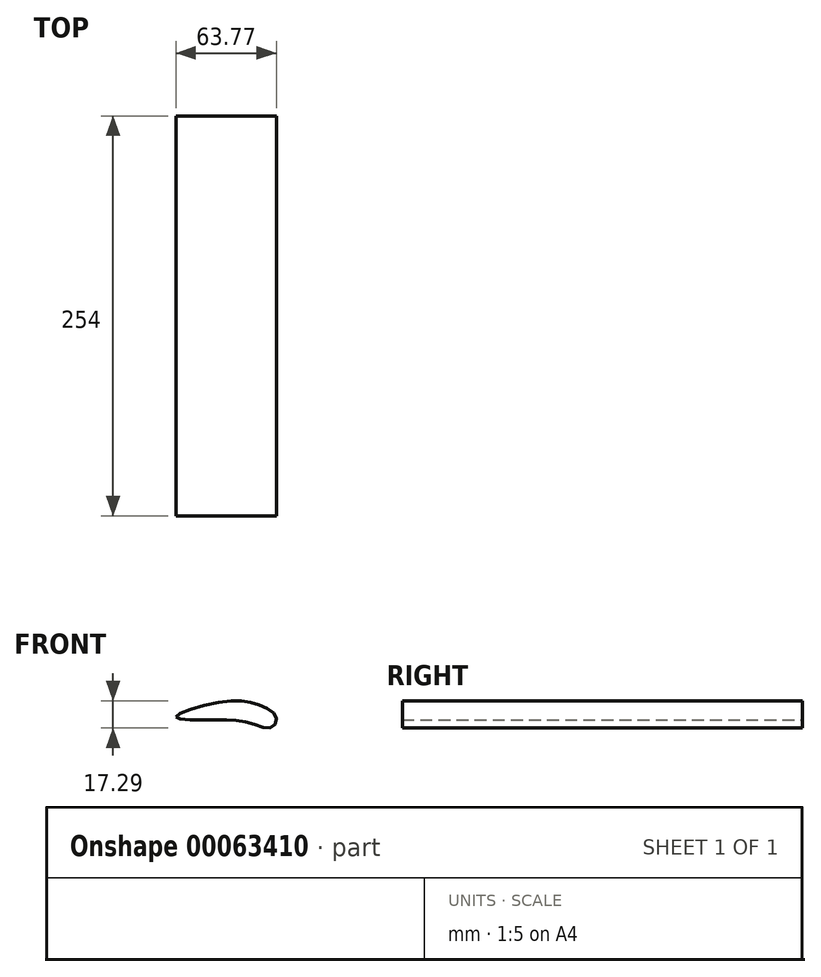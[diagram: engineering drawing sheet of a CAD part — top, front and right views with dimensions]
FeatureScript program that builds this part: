
annotation { "Feature Type Name" : "Feature", "Feature Type Description" : "" }
export const myFeature = defineFeature(function(context is Context, id is Id, definition is map)
    precondition{}
    {
        {
            var Q0;
            Q0=qCreatedBy(makeId("Front.planeOp"),FACE);
            var sketch = newSketch(context, id + "F0", { "sketchPlane" : qUnion([Q0])});
            skFitSpline(sketch, "E0", {"points": [v(0, 0) * mm, v(28.44, 9.25) * mm, v(51.9, 7.87) * mm, v(63.5, 0) * mm, v(60.74, -6.76) * mm, v(45.83, -3.73) * mm, v(21.26, -2.07) * mm, v(0, 0) * mm]});
            skSolve(sketch);
        }
        {
            var Q0;
            Q0=qSketchRegion(id+"F0",true);
            extrude(context, id + "F1", {"entities" : qUnion([Q0]), "depth" : 254 * mm});
        }
    });
